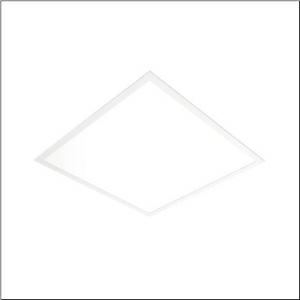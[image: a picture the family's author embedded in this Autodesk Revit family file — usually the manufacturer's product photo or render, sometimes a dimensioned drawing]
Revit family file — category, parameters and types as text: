
# Revit family: apollon_r__41_51mh11w72443_9aaa
name_source: partatom
category: Lighting Fixtures
units: mm (PartAtom-declared; Revit-internal decimal feet)

## family parameters
Cut with Voids When Loaded = No
Host = Face
Light Source = No
Part Type = Normal
Room Calculation Point = No
Round Connector Dimension = Use Diameter
Shared = No

## types (1)
- Apollon® 41 (1 x LED, 3700 lm, 28.5 W, 4000K)
    Apparent Load = 29 VA
    CIE Flux Codes = 61 87 97 100 100
    Color Rendering = 80
    Color Temperature = 4000K
    Default Elevation = 1800 mm
    Description = Apollon® 41, office luminaire, primary optical cover: prismatic diffuser, of PS, light emission: direct distribution, primary light characteristic: symmetric, installation type: lay-in mounting, LED, rated luminous flux: 3.700lm, luminous efficacy: 130lm/W, light colour: 840, colour temperature: 4000K, control gear: ON/OFF, with terminal, 3-pole, mains connection: 220..240V, AC, 50/60Hz, housing, of aluminium section, traffic white (RAL 9016), module: M625, length: 620mm, width: 620mm, height: 60mm, recess depth: 180mm, housing upper side, of sheet steel, protection rating (complete): IP20, protection rating (lamp compartment, on room side): IP40, insulation class (complete): insulation class II (safety insulation), certification: CE, ENEC, impact resistance: IK03, permissible operating ambient temperature: -25..+40°C, packaging unit: 1 piece
    Height = 0 mm  [stored 0 ft]
    Lamp = 1 x LED
    Lamp Light Flux = 3700 lm
    Lamp Power = 28.5 W
    Lamp count = 1
    Length = 620 mm
    Luminous efficacy = 130 lm/W
    Manufacturer = Siteco
    ModVariant = No
    Model = 51MH11W72443
    Mounting Place = Ceiling
    Mounting Type = Recessed
    Number of Poles = 1
    OnlyDefault = Yes
    Power Factor = 1
    Product Name = Apollon® 41
    Product group = office luminaire | ceiling recessed
    ProductGroupID = 401
    Protection Class = Protection class II
    Protection Degree = IP 20
    RLX_Detail_Level = 1
    RLX_Emergency_Light_Flux = 0 lm
    RLX_Emergency_Type = 0
    RLX_Emergency_Type_DB = No
    RlxData = <blob elided: 12265 chars, md5=515b8b39>
    Socket = socket
    Standby Power = 0 W
    System Light Flux = 3700 lm
    System Power = 29 W
    Type Comments = Product without accessories
    Type Image = l_1291024.jpg
    URL = http://relux.com
    VarID = ---
    Voltage = 0 V
    Weight = 0.00 kg
    Width = 620 mm

note: [stored X ft] marks values corroborated as IEEE doubles in the binary element streams (Revit-internal decimal feet)

## geometry (parser evidence)
native form markers: Sweep x10
no freeform markers — native parametric forms only
